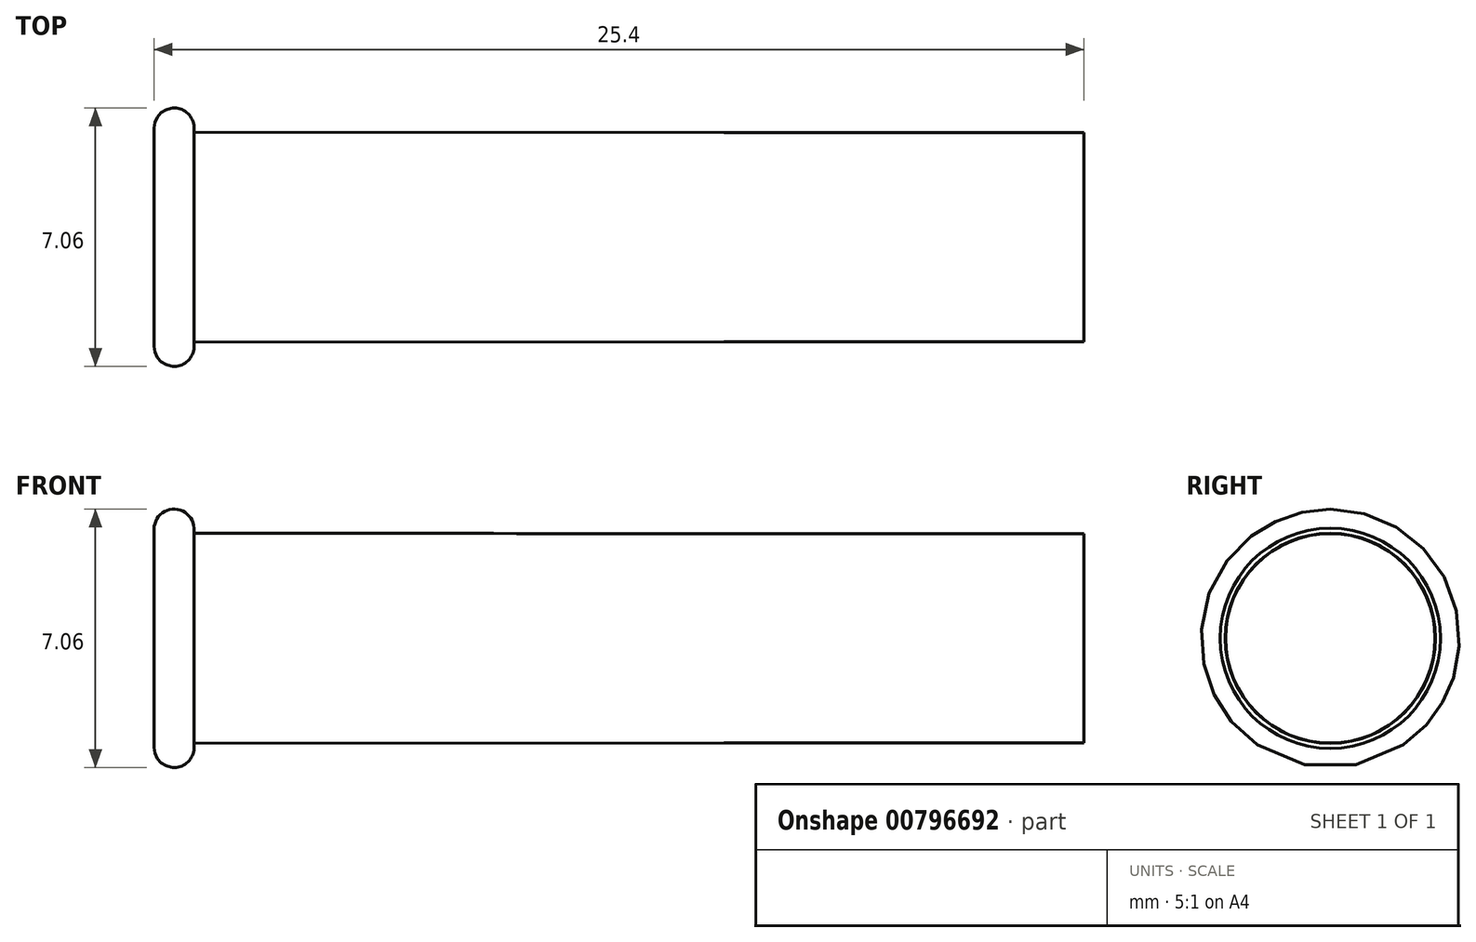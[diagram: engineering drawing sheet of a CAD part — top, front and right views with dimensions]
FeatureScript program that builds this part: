
annotation { "Feature Type Name" : "Feature", "Feature Type Description" : "" }
export const myFeature = defineFeature(function(context is Context, id is Id, definition is map)
    precondition{}
    {
        {
            var Q0;
            Q0=qCreatedBy(makeId("Front.planeOp"),FACE);
            var sketch = newSketch(context, id + "F0", { "sketchPlane" : qUnion([Q0])});
            skLineSegment(sketch, "E0", {"start": v(0, 0) * mm, "end": v(1.09, 0) * mm});
            skLineSegment(sketch, "E1", {"start": v(1.09, 0) * mm, "end": v(15.57, 0) * mm});
            skLineSegment(sketch, "E2", {"start": v(0, -4.63) * mm, "end": v(15.57, -4.63) * mm});
            skLineSegment(sketch, "E3", {"start": v(0, -7.61) * mm, "end": v(25.4, -7.61) * mm});
            skLineSegment(sketch, "E4", {"start": v(15.57, 0) * mm, "end": v(25.4, 0) * mm});
            skLineSegment(sketch, "E5", {"start": v(25.4, 0) * mm, "end": v(25.4, 2.86) * mm});
            skLineSegment(sketch, "E6", {"start": v(25.4, 2.86) * mm, "end": v(15.57, 2.86) * mm});
            skLineSegment(sketch, "E7", {"start": v(15.57, 2.86) * mm, "end": v(1.09, 2.87) * mm});
            skLineSegment(sketch, "E8", {"start": v(1.09, 2.87) * mm, "end": v(1.09, 0) * mm});
            skLineSegment(sketch, "E9", {"start": v(0, 0) * mm, "end": v(0, 3.53) * mm});
            skLineSegment(sketch, "E10", {"start": v(0.54, 0) * mm, "end": v(0.54, 3.53) * mm});
            skCircle(sketch, "E11", {"center": v(0.54, 2.98) * mm, "radius": 0.54 * mm});
            skLineSegment(sketch, "E12", {"start": v(1.09, 2.87) * mm, "end": v(1.09, 3) * mm});
            skSolve(sketch);
        }
        {
            var Q0;
            {var subQ0=sQuery(id+"F0.wireOp",EDGE,"E9");var subQ1=sQuery(id+"F0.wireOp",EDGE,"E0");var subQ2=makeQuery(id+"F0.imprint","INTERSECT",VERTEX,{"derivedFrom":[subQ1,subQ0]});Q0=makeQuery(id+"F0.imprint","IMPRINT",FACE,{"disambiguationData":[TD([[makeQuery(id+"F0.imprint","IMPRINT",EDGE,{"disambiguationData":[TD([[subQ2,-1.0]])],"derivedFrom":subQ1}),1.0]])]});}
            var Q1;
            {var subQ0=sQuery(id+"F0.wireOp",EDGE,"E11");var subQ1=sQuery(id+"F0.wireOp",EDGE,"E10");var subQ2=makeQuery(id+"F0.imprint","INTERSECT",VERTEX,{"disambiguationData":[OD(0.0)],"derivedFrom":[subQ1,subQ0]});Q1=makeQuery(id+"F0.imprint","IMPRINT",FACE,{"disambiguationData":[TD([[makeQuery(id+"F0.imprint","IMPRINT",EDGE,{"disambiguationData":[TD([[subQ2,1.0]])],"derivedFrom":subQ1}),1.0]])]});}
            var Q2;
            {var subQ0=sQuery(id+"F0.wireOp",EDGE,"E11");var subQ1=sQuery(id+"F0.wireOp",EDGE,"E10");var subQ2=makeQuery(id+"F0.imprint","INTERSECT",VERTEX,{"disambiguationData":[OD(0.0)],"derivedFrom":[subQ1,subQ0]});Q2=makeQuery(id+"F0.imprint","IMPRINT",FACE,{"disambiguationData":[TD([[makeQuery(id+"F0.imprint","IMPRINT",EDGE,{"disambiguationData":[TD([[subQ2,1.0]])],"derivedFrom":subQ1}),-1.0]])]});}
            var Q3;
            {var subQ7=sQuery(id+"F0.wireOp",EDGE,"E8");Q3=makeQuery(id+"F0.imprint","IMPRINT",FACE,{"disambiguationData":[TD([[makeQuery(id+"F0.imprint","IMPRINT",EDGE,{"derivedFrom":subQ7}),-1.0]])]});}
            var Q4;
            Q4=makeQuery(id+"F0.imprint","IMPRINT",FACE,{"disambiguationData":[TD([[makeQuery(id+"F0.imprint","IMPRINT",EDGE,{"derivedFrom":sQuery(id+"F0.wireOp",EDGE,"E1")}),1.0]])]});
            var Q5;
            Q5=sQuery(id+"F0.wireOp",EDGE,"E1");
            revolve(context, id + "F1", {"surfaceOperationType" : NewSurfaceOperationType.NEW, "entities" : qUnion([Q0, Q1, Q2, Q3, Q4]), "axis" : qUnion([Q5]), "revolveType" : RevolveType.FULL});
        }
    });
